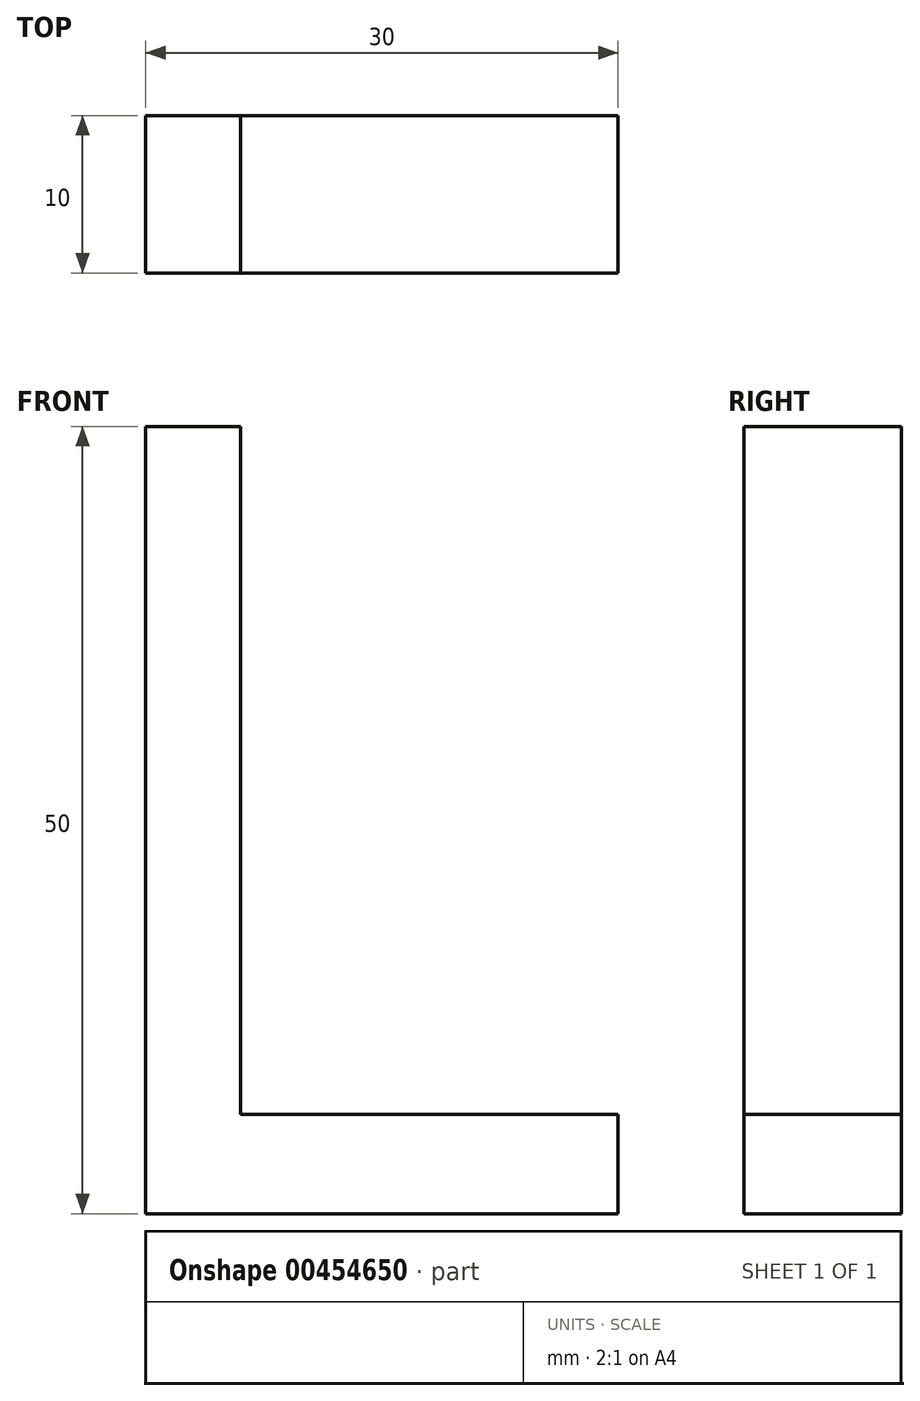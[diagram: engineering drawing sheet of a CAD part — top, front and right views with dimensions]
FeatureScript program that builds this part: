
annotation { "Feature Type Name" : "Feature", "Feature Type Description" : "" }
export const myFeature = defineFeature(function(context is Context, id is Id, definition is map)
    precondition{}
    {
        {
            var Q0;
            Q0=qCreatedBy(makeId("Front.planeOp"),FACE);
            var sketch = newSketch(context, id + "F0", { "sketchPlane" : qUnion([Q0])});
            skLineSegment(sketch, "E0.bottom", {"start": v(0, 21.6) * mm, "end": v(6.03, 21.6) * mm});
            skLineSegment(sketch, "E0.top", {"start": v(0, -28.25) * mm, "end": v(6.03, -28.25) * mm});
            skLineSegment(sketch, "E0.left", {"start": v(0, 21.6) * mm, "end": v(0, -28.25) * mm});
            skLineSegment(sketch, "E0.right", {"start": v(6.03, 21.6) * mm, "end": v(6.03, -22.09) * mm});
            skLineSegment(sketch, "E1.bottom", {"start": v(6.03, -22.09) * mm, "end": v(30, -22.09) * mm});
            skLineSegment(sketch, "E1.top", {"start": v(0, -28.4) * mm, "end": v(30, -28.4) * mm});
            skLineSegment(sketch, "E1.left", {"start": v(0, -22.09) * mm, "end": v(0, -28.4) * mm});
            skLineSegment(sketch, "E1.right", {"start": v(30, -22.09) * mm, "end": v(30, -28.4) * mm});
            skSolve(sketch);
        }
        {
            var Q0;
            Q0 = qSketchRegion(id + "F0", true);
            extrude(context, id + "F1", {"entities" : qUnion([Q0]), "depth" : 10 * mm, "offsetDistance" : 25 * mm});
        }
    });
